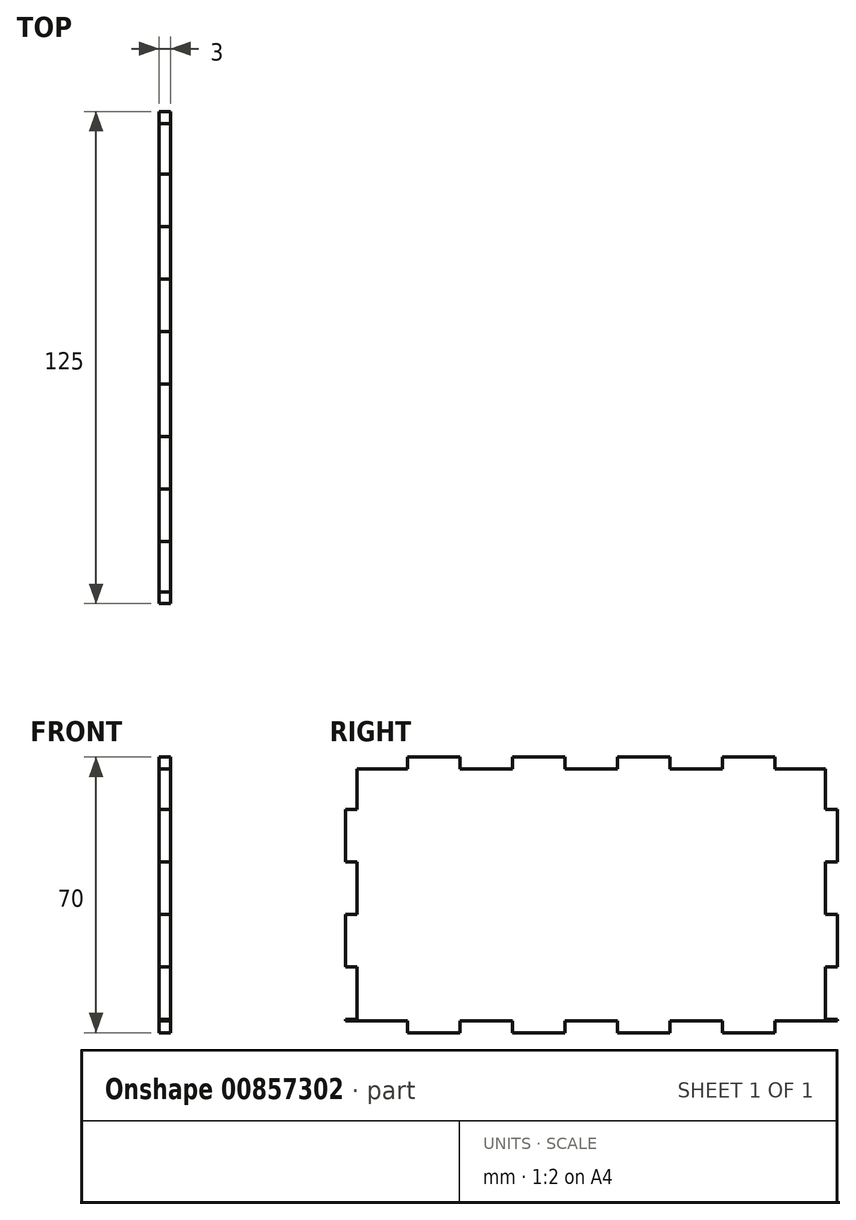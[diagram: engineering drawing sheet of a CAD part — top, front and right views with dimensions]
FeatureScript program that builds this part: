
annotation { "Feature Type Name" : "Feature", "Feature Type Description" : "" }
export const myFeature = defineFeature(function(context is Context, id is Id, definition is map)
    precondition{}
    {
        {
            var Q0;
            Q0=qCreatedBy(makeId("Right.planeOp"),FACE);
            var sketch = newSketch(context, id + "F0", { "sketchPlane" : qUnion([Q0])});
            skLineSegment(sketch, "E0.bottom", {"start": v(-62.5, -35) * mm, "end": v(62.5, -35) * mm});
            skLineSegment(sketch, "E0.top", {"start": v(-62.5, 35) * mm, "end": v(62.5, 35) * mm});
            skLineSegment(sketch, "E0.left", {"start": v(-62.5, -35) * mm, "end": v(-62.5, 35) * mm});
            skLineSegment(sketch, "E0.right", {"start": v(62.5, -35) * mm, "end": v(62.5, 35) * mm});
            skPoint(sketch, "E0.middle", {"position": v(0, 0) * mm});
            skSolve(sketch);
        }
        {
            var Q0;
            Q0=makeQuery(id+"F0.imprint","IMPRINT",FACE,{"disambiguationData":[TD([[makeQuery(id+"F0.imprint","IMPRINT",EDGE,{"derivedFrom":sQuery(id+"F0.wireOp",EDGE,"E0.bottom")}),1.0]])]});
            extrude(context, id + "F1", {"entities" : qUnion([Q0]), "depth" : 3 * mm, "offsetDistance" : 25 * mm});
        }
        {
            var Q0;
            Q0=makeQuery(id+"F1.opExtrude","CAP_FACE",FACE,{"disambiguationData":[OSD([sQuery(id+"F0.wireOp",EDGE,"E0.bottom"),sQuery(id+"F0.wireOp",EDGE,"E0.top"),sQuery(id+"F0.wireOp",EDGE,"E0.left"),sQuery(id+"F0.wireOp",EDGE,"E0.right")])],"isStart":true});
            var sketch = newSketch(context, id + "F2", { "sketchPlane" : qUnion([Q0])});
            skLineSegment(sketch, "E1.bottom", {"start": v(-62.5, 35) * mm, "end": v(-46.66, 35) * mm});
            skLineSegment(sketch, "E1.top", {"start": v(-62.5, 32) * mm, "end": v(-46.66, 32) * mm});
            skLineSegment(sketch, "E1.left", {"start": v(-62.5, 35) * mm, "end": v(-62.5, 32) * mm});
            skLineSegment(sketch, "E1.right", {"start": v(-46.66, 35) * mm, "end": v(-46.66, 32) * mm});
            skLineSegment(sketch, "E2.bottom", {"start": v(-33.33, 35) * mm, "end": v(-20, 35) * mm});
            skLineSegment(sketch, "E2.top", {"start": v(-33.33, 32) * mm, "end": v(-20, 32) * mm});
            skLineSegment(sketch, "E2.left", {"start": v(-33.33, 35) * mm, "end": v(-33.33, 32) * mm});
            skLineSegment(sketch, "E2.right", {"start": v(-20, 35) * mm, "end": v(-20, 32) * mm});
            skLineSegment(sketch, "E3.bottom", {"start": v(-6.66, 35) * mm, "end": v(6.67, 35) * mm});
            skLineSegment(sketch, "E3.top", {"start": v(-6.66, 32) * mm, "end": v(6.67, 32) * mm});
            skLineSegment(sketch, "E3.left", {"start": v(-6.66, 35) * mm, "end": v(-6.66, 32) * mm});
            skLineSegment(sketch, "E3.right", {"start": v(6.67, 35) * mm, "end": v(6.67, 32) * mm});
            skLineSegment(sketch, "E4", {"start": v(0, 35) * mm, "end": v(0, -35) * mm, "construction": true});
            skLineSegment(sketch, "E5.MirrorCS", {"start": v(6.66, 35) * mm, "end": v(6.66, 32) * mm});
            skLineSegment(sketch, "E6.MirrorCS", {"start": v(20, 35) * mm, "end": v(20, 32) * mm});
            skLineSegment(sketch, "E7.MirrorCS", {"start": v(46.66, 35) * mm, "end": v(46.66, 32) * mm});
            skLineSegment(sketch, "E8.MirrorCS", {"start": v(62.5, 35) * mm, "end": v(62.5, 32) * mm});
            skLineSegment(sketch, "E9.MirrorCS", {"start": v(-6.67, 35) * mm, "end": v(-6.67, 32) * mm});
            skLineSegment(sketch, "E10.MirrorCS", {"start": v(33.33, 35) * mm, "end": v(33.33, 32) * mm});
            skLineSegment(sketch, "E11.MirrorCS", {"start": v(62.5, 35) * mm, "end": v(46.66, 35) * mm});
            skLineSegment(sketch, "E12.MirrorCS", {"start": v(6.66, 32) * mm, "end": v(-6.67, 32) * mm});
            skLineSegment(sketch, "E13.MirrorCS", {"start": v(33.33, 32) * mm, "end": v(20, 32) * mm});
            skLineSegment(sketch, "E14.MirrorCS", {"start": v(6.66, 35) * mm, "end": v(-6.67, 35) * mm});
            skLineSegment(sketch, "E15.MirrorCS", {"start": v(62.5, 32) * mm, "end": v(46.66, 32) * mm});
            skLineSegment(sketch, "E16.MirrorCS", {"start": v(33.33, 35) * mm, "end": v(20, 35) * mm});
            skLineSegment(sketch, "E17.bottom", {"start": v(-62.5, 35) * mm, "end": v(-59.5, 35) * mm});
            skLineSegment(sketch, "E17.top", {"start": v(-62.5, 21.67) * mm, "end": v(-59.5, 21.67) * mm});
            skLineSegment(sketch, "E17.left", {"start": v(-62.5, 35) * mm, "end": v(-62.5, 21.67) * mm});
            skLineSegment(sketch, "E17.right", {"start": v(-59.5, 35) * mm, "end": v(-59.5, 21.67) * mm});
            skLineSegment(sketch, "E18.0.1.0", {"start": v(-62.5, -5) * mm, "end": v(-59.5, -5) * mm});
            skLineSegment(sketch, "E18.0.1.1", {"start": v(-62.5, 8.33) * mm, "end": v(-62.5, -5) * mm});
            skLineSegment(sketch, "E18.0.1.2", {"start": v(-62.5, 8.33) * mm, "end": v(-62.5, 5.33) * mm});
            skLineSegment(sketch, "E18.0.1.3", {"start": v(-62.5, 8.33) * mm, "end": v(-59.5, 8.33) * mm});
            skLineSegment(sketch, "E18.0.1.4", {"start": v(-59.5, 8.33) * mm, "end": v(-59.5, -5) * mm});
            skLineSegment(sketch, "E18.0.2.0", {"start": v(-62.5, -31.67) * mm, "end": v(-59.5, -31.67) * mm});
            skLineSegment(sketch, "E18.0.2.1", {"start": v(-62.5, -18.33) * mm, "end": v(-62.5, -31.67) * mm});
            skLineSegment(sketch, "E18.0.2.2", {"start": v(-62.5, -18.33) * mm, "end": v(-62.5, -21.33) * mm});
            skLineSegment(sketch, "E18.0.2.3", {"start": v(-62.5, -18.33) * mm, "end": v(-59.5, -18.33) * mm});
            skLineSegment(sketch, "E18.0.2.4", {"start": v(-59.5, -18.33) * mm, "end": v(-59.5, -31.67) * mm});
            skLineSegment(sketch, "E18.direction1", {"start": v(-62.5, 21.67) * mm, "end": v(-37.5, 21.67) * mm, "construction": true});
            skLineSegment(sketch, "E18.direction2", {"start": v(-62.5, 21.67) * mm, "end": v(-62.5, -5) * mm, "construction": true});
            skLineSegment(sketch, "E19.MirrorCS", {"start": v(62.5, -31.67) * mm, "end": v(59.5, -31.67) * mm});
            skLineSegment(sketch, "E20.MirrorCS", {"start": v(62.5, -5) * mm, "end": v(59.5, -5) * mm});
            skLineSegment(sketch, "E21.MirrorCS", {"start": v(62.5, 21.67) * mm, "end": v(59.5, 21.67) * mm});
            skLineSegment(sketch, "E22.MirrorCS", {"start": v(62.5, -18.33) * mm, "end": v(59.5, -18.33) * mm});
            skLineSegment(sketch, "E23.MirrorCS", {"start": v(62.5, 35) * mm, "end": v(59.5, 35) * mm});
            skLineSegment(sketch, "E24.MirrorCS", {"start": v(62.5, 8.33) * mm, "end": v(59.5, 8.33) * mm});
            skLineSegment(sketch, "E25.MirrorCS", {"start": v(62.5, -18.33) * mm, "end": v(62.5, -21.33) * mm});
            skLineSegment(sketch, "E26.MirrorCS", {"start": v(62.5, 8.33) * mm, "end": v(62.5, 5.33) * mm});
            skLineSegment(sketch, "E27.MirrorCS", {"start": v(62.5, 8.33) * mm, "end": v(62.5, -5) * mm});
            skLineSegment(sketch, "E28.MirrorCS", {"start": v(62.5, 21.67) * mm, "end": v(62.5, -5) * mm, "construction": true});
            skLineSegment(sketch, "E29.MirrorCS", {"start": v(59.5, -18.33) * mm, "end": v(59.5, -31.67) * mm});
            skLineSegment(sketch, "E30.MirrorCS", {"start": v(62.5, -18.33) * mm, "end": v(62.5, -31.67) * mm});
            skLineSegment(sketch, "E31.MirrorCS", {"start": v(59.5, 35) * mm, "end": v(59.5, 21.67) * mm});
            skLineSegment(sketch, "E32.MirrorCS", {"start": v(62.5, 35) * mm, "end": v(62.5, 21.67) * mm});
            skLineSegment(sketch, "E33.MirrorCS", {"start": v(59.5, 8.33) * mm, "end": v(59.5, -5) * mm});
            skLineSegment(sketch, "E34", {"start": v(-62.5, 0) * mm, "end": v(62.5, 0) * mm, "construction": true});
            skLineSegment(sketch, "E35.MirrorCS", {"start": v(-6.66, -35) * mm, "end": v(-6.66, -32) * mm});
            skLineSegment(sketch, "E36.MirrorCS", {"start": v(6.67, -35) * mm, "end": v(6.67, -32) * mm});
            skLineSegment(sketch, "E37.MirrorCS", {"start": v(6.66, -35) * mm, "end": v(6.66, -32) * mm});
            skLineSegment(sketch, "E38.MirrorCS", {"start": v(-6.67, -35) * mm, "end": v(-6.67, -32) * mm});
            skLineSegment(sketch, "E39.MirrorCS", {"start": v(62.5, -35) * mm, "end": v(62.5, -32) * mm});
            skLineSegment(sketch, "E40.MirrorCS", {"start": v(46.66, -35) * mm, "end": v(46.66, -32) * mm});
            skLineSegment(sketch, "E41.MirrorCS", {"start": v(-62.5, -35) * mm, "end": v(-59.5, -35) * mm});
            skLineSegment(sketch, "E42.MirrorCS", {"start": v(-46.66, -35) * mm, "end": v(-46.66, -32) * mm});
            skLineSegment(sketch, "E43.MirrorCS", {"start": v(-33.33, -35) * mm, "end": v(-33.33, -32) * mm});
            skLineSegment(sketch, "E44.MirrorCS", {"start": v(-62.5, -35) * mm, "end": v(-62.5, -32) * mm});
            skLineSegment(sketch, "E45.MirrorCS", {"start": v(20, -35) * mm, "end": v(20, -32) * mm});
            skLineSegment(sketch, "E46.MirrorCS", {"start": v(33.33, -35) * mm, "end": v(33.33, -32) * mm});
            skLineSegment(sketch, "E47.MirrorCS", {"start": v(-20, -35) * mm, "end": v(-20, -32) * mm});
            skLineSegment(sketch, "E48.MirrorCS", {"start": v(62.5, -35) * mm, "end": v(59.5, -35) * mm});
            skLineSegment(sketch, "E49.MirrorCS", {"start": v(-6.66, -32) * mm, "end": v(6.67, -32) * mm});
            skLineSegment(sketch, "E50.MirrorCS", {"start": v(-6.66, -35) * mm, "end": v(6.67, -35) * mm});
            skLineSegment(sketch, "E51.MirrorCS", {"start": v(-62.5, -35) * mm, "end": v(-46.66, -35) * mm});
            skLineSegment(sketch, "E52.MirrorCS", {"start": v(6.66, -32) * mm, "end": v(-6.67, -32) * mm});
            skLineSegment(sketch, "E53.MirrorCS", {"start": v(33.33, -35) * mm, "end": v(20, -35) * mm});
            skLineSegment(sketch, "E54.MirrorCS", {"start": v(-33.33, -35) * mm, "end": v(-20, -35) * mm});
            skLineSegment(sketch, "E55.MirrorCS", {"start": v(62.5, -32) * mm, "end": v(46.66, -32) * mm});
            skLineSegment(sketch, "E56.MirrorCS", {"start": v(-62.5, -32) * mm, "end": v(-46.66, -32) * mm});
            skLineSegment(sketch, "E57.MirrorCS", {"start": v(62.5, -35) * mm, "end": v(46.66, -35) * mm});
            skLineSegment(sketch, "E58.MirrorCS", {"start": v(33.33, -32) * mm, "end": v(20, -32) * mm});
            skLineSegment(sketch, "E59.MirrorCS", {"start": v(6.66, -35) * mm, "end": v(-6.67, -35) * mm});
            skLineSegment(sketch, "E60.MirrorCS", {"start": v(-33.33, -32) * mm, "end": v(-20, -32) * mm});
            skSolve(sketch);
        }
        {
            var Q0;
            Q0 = qSketchRegion(id + "F2", true);
            extrude(context, id + "F3", {"entities" : qUnion([Q0]), "operationType" : NewBodyOperationType.REMOVE, "endBound" : BoundingType.THROUGH_ALL, "oppositeDirection" : true, "depth" : 25 * mm, "offsetDistance" : 25 * mm});
        }
    });
